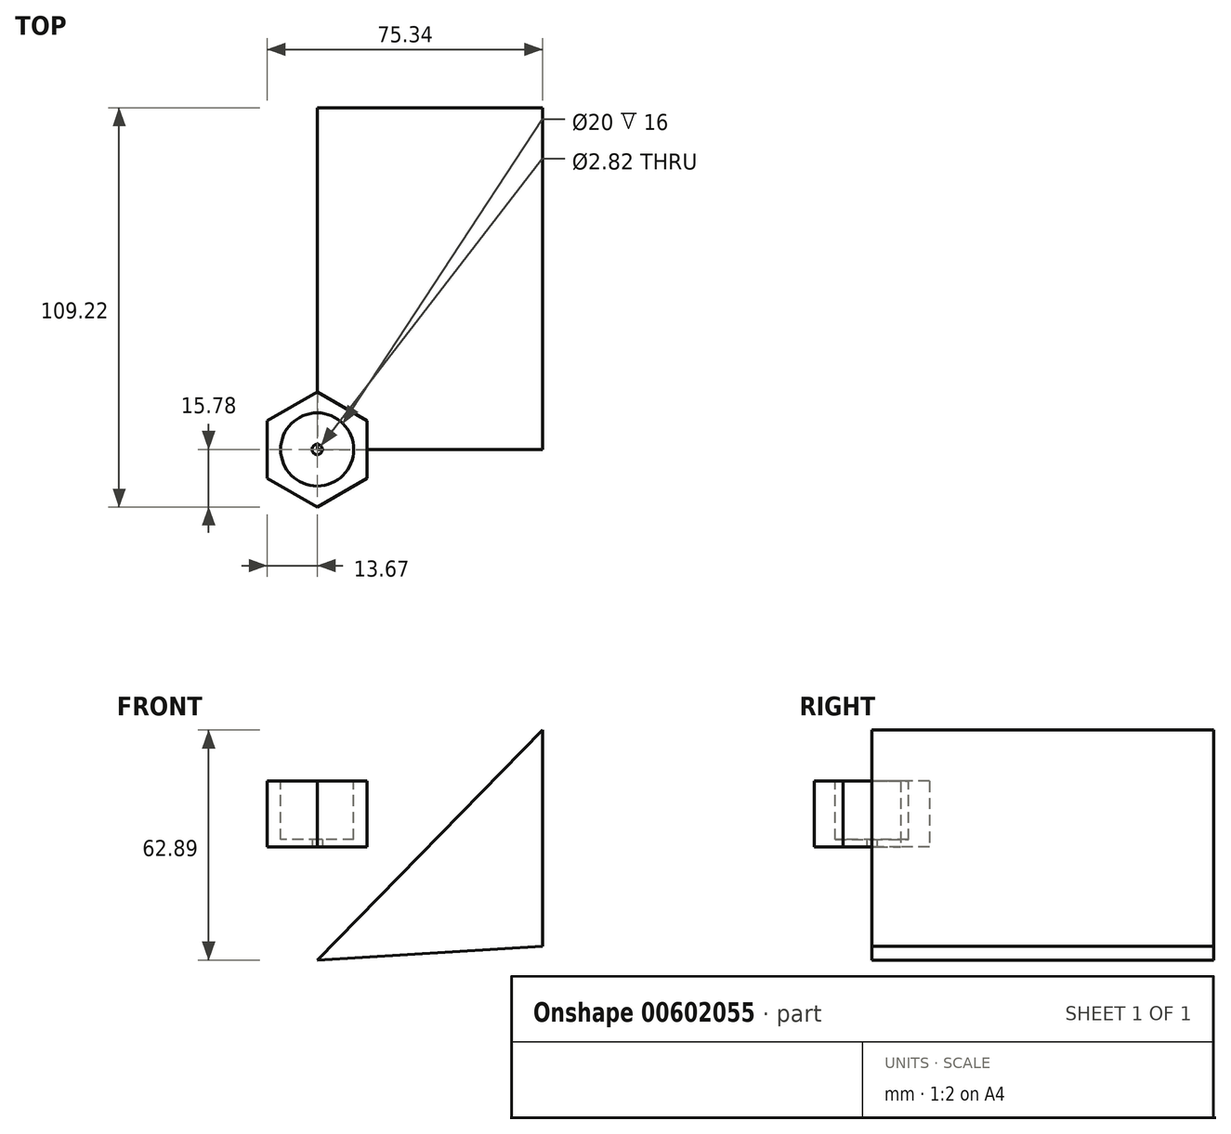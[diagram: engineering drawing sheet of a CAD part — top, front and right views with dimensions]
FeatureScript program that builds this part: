
annotation { "Feature Type Name" : "Feature", "Feature Type Description" : "" }
export const myFeature = defineFeature(function(context is Context, id is Id, definition is map)
    precondition{}
    {
        {
            var Q0;
            Q0=qCreatedBy(makeId("Top.planeOp"),FACE);
            var sketch = newSketch(context, id + "F0", { "sketchPlane" : qUnion([Q0])});
            skCircle(sketch, "E0", {"center": v(0, 0) * mm, "radius": 10 * mm});
            skCircle(sketch, "E1.cCircle", {"center": v(0, 0) * mm, "radius": 13.67 * mm, "construction": true});
            skLineSegment(sketch, "E1.0", {"start": v(13.67, 7.89) * mm, "end": v(13.67, -7.89) * mm});
            skLineSegment(sketch, "E1.1", {"start": v(13.67, -7.89) * mm, "end": v(0, -15.78) * mm});
            skLineSegment(sketch, "E1.2", {"start": v(0, -15.78) * mm, "end": v(-13.67, -7.89) * mm});
            skLineSegment(sketch, "E1.3", {"start": v(-13.67, -7.89) * mm, "end": v(-13.67, 7.89) * mm});
            skLineSegment(sketch, "E1.4", {"start": v(-13.67, 7.89) * mm, "end": v(0, 15.78) * mm});
            skLineSegment(sketch, "E1.5", {"start": v(0, 15.78) * mm, "end": v(13.67, 7.89) * mm});
            skPoint(sketch, "E1.0.midPoint", {"position": v(13.67, 0) * mm});
            skSolve(sketch);
        }
        {
            var Q0;
            Q0=makeQuery(id+"F0.imprint","IMPRINT",FACE,{"disambiguationData":[TD([[makeQuery(id+"F0.imprint","IMPRINT",EDGE,{"derivedFrom":sQuery(id+"F0.wireOp",EDGE,"E0")}),-1.0]])]});
            var Q1;
            Q1=makeQuery(id+"F0.imprint","IMPRINT",FACE,{"disambiguationData":[TD([[makeQuery(id+"F0.imprint","IMPRINT",EDGE,{"derivedFrom":sQuery(id+"F0.wireOp",EDGE,"E0")}),1.0]])]});
            extrude(context, id + "F1", {"entities" : qUnion([Q0, Q1]), "depth" : 18 * mm, "offsetDistance" : 25 * mm});
        }
        {
            var Q0;
            Q0=makeQuery(id+"F1.opExtrude","CAP_FACE",FACE,{"disambiguationData":[OSD([sQuery(id+"F0.wireOp",EDGE,"E1.0"),sQuery(id+"F0.wireOp",EDGE,"E1.1"),sQuery(id+"F0.wireOp",EDGE,"E1.2"),sQuery(id+"F0.wireOp",EDGE,"E1.3"),sQuery(id+"F0.wireOp",EDGE,"E1.4"),sQuery(id+"F0.wireOp",EDGE,"E1.5")])],"isStart":false});
            var sketch = newSketch(context, id + "F2", { "sketchPlane" : qUnion([Q0])});
            skCircle(sketch, "E2", {"center": v(0, 0) * mm, "radius": 10 * mm});
            skSolve(sketch);
        }
        {
            var Q0;
            Q0 = qSketchRegion(id + "F2", true);
            extrude(context, id + "F3", {"entities" : qUnion([Q0]), "operationType" : NewBodyOperationType.REMOVE, "oppositeDirection" : true, "depth" : 16 * mm, "offsetDistance" : 25 * mm});
        }
        {
            var Q0;
            Q0=makeQuery(id+"F1.opExtrude","CAP_FACE",FACE,{"disambiguationData":[OSD([sQuery(id+"F0.wireOp",EDGE,"E1.0"),sQuery(id+"F0.wireOp",EDGE,"E1.1"),sQuery(id+"F0.wireOp",EDGE,"E1.2"),sQuery(id+"F0.wireOp",EDGE,"E1.3"),sQuery(id+"F0.wireOp",EDGE,"E1.4"),sQuery(id+"F0.wireOp",EDGE,"E1.5")])],"isStart":true});
            var sketch = newSketch(context, id + "F4", { "sketchPlane" : qUnion([Q0])});
            skCircle(sketch, "E3", {"center": v(0, 0) * mm, "radius": 1.4 * mm});
            skSolve(sketch);
        }
        {
            var Q0;
            Q0 = qSketchRegion(id + "F4", true);
            extrude(context, id + "F5", {"entities" : qUnion([Q0]), "operationType" : NewBodyOperationType.REMOVE, "oppositeDirection" : true, "depth" : 25 * mm, "offsetDistance" : 25 * mm});
        }
        {
            var Q0;
            Q0=qCreatedBy(makeId("Front.planeOp"),FACE);
            var sketch = newSketch(context, id + "F6", { "sketchPlane" : qUnion([Q0])});
            skLineSegment(sketch, "E4", {"start": v(0, -30.92) * mm, "end": v(61.67, 31.97) * mm});
            skLineSegment(sketch, "E5", {"start": v(61.67, 31.97) * mm, "end": v(61.67, -27.22) * mm});
            skLineSegment(sketch, "E6", {"start": v(61.67, -27.22) * mm, "end": v(0, -30.92) * mm});
            skSolve(sketch);
        }
        {
            var Q0;
            Q0=makeQuery(id+"F6.imprint","IMPRINT",FACE,{"disambiguationData":[TD([[makeQuery(id+"F6.imprint","IMPRINT",EDGE,{"derivedFrom":sQuery(id+"F6.wireOp",EDGE,"E4")}),-1.0]])]});
            extrude(context, id + "F7", {"entities" : qUnion([Q0]), "oppositeDirection" : true, "depth" : 93.44 * mm, "offsetDistance" : 25 * mm});
        }
    });
